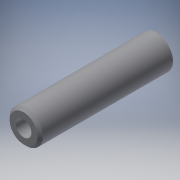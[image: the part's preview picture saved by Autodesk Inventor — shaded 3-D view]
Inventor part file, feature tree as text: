
AUTODESK INVENTOR PART (.ipt)
format: ipt  version: 2016 (Build 200138000, 138)  size: 98,304 bytes
history: native  units: mm
features: extrude x1, chamfer x1, sketch x1
ambient origin geometry x8: Origin, YZ Plane, XZ Plane, XY Plane, X Axis, Y Axis, Z Axis, Center Point
bodies: Solid1 (feature_tree)
feature tree (3):
  extrude  "Extrusion1"  Depth=2.0mm
  chamfer  "Chamfer1"  Distance=200.0mm
  sketch  "Sketch1"  dims[d0=50.0mm d1=23.5mm d2=200.0mm d3=0.0mm d4=4.0mm d5=2.0mm d6=45.0deg]
